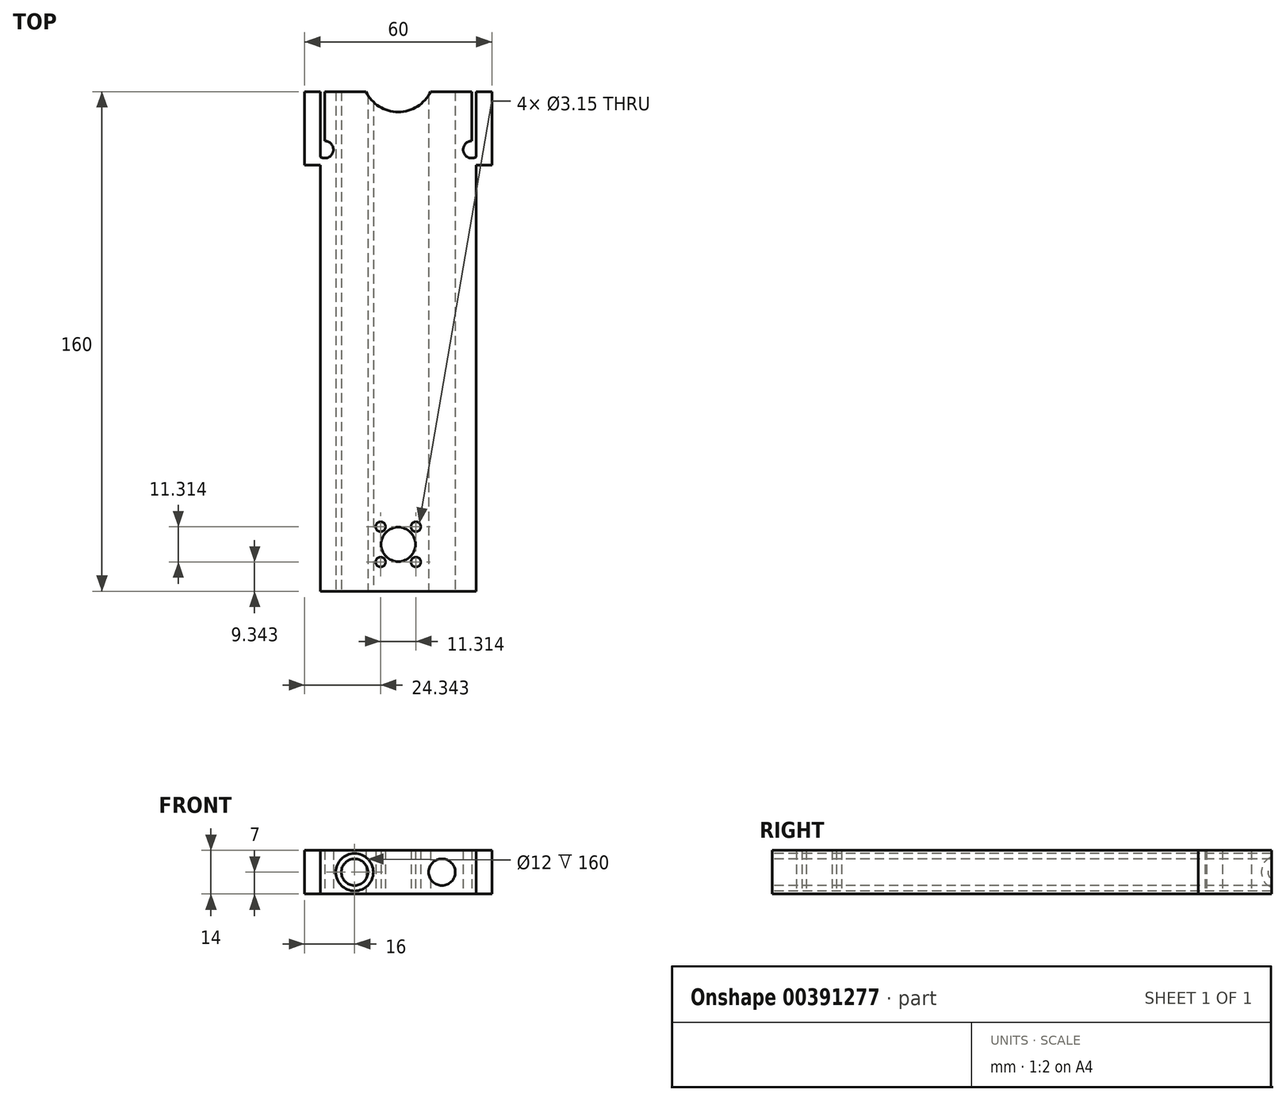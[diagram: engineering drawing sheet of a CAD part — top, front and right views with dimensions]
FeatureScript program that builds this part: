
annotation { "Feature Type Name" : "Feature", "Feature Type Description" : "" }
export const myFeature = defineFeature(function(context is Context, id is Id, definition is map)
    precondition{}
    {
        {
            var Q0;
            Q0=qCreatedBy(makeId("Top.planeOp"),FACE);
            var sketch = newSketch(context, id + "F0", { "sketchPlane" : qUnion([Q0])});
            skPoint(sketch, "E0", {"position": v(0, 0) * mm});
            skLineSegment(sketch, "E1.bottom", {"start": v(5.66, -5.66) * mm, "end": v(-5.66, -5.66) * mm, "construction": true});
            skLineSegment(sketch, "E1.top", {"start": v(5.66, 5.66) * mm, "end": v(-5.66, 5.66) * mm, "construction": true});
            skLineSegment(sketch, "E1.left", {"start": v(5.66, -5.66) * mm, "end": v(5.66, 5.66) * mm, "construction": true});
            skLineSegment(sketch, "E1.right", {"start": v(-5.66, -5.66) * mm, "end": v(-5.66, 5.66) * mm, "construction": true});
            skCircle(sketch, "E2", {"center": v(-5.66, 5.66) * mm, "radius": 1.57 * mm});
            skCircle(sketch, "E3", {"center": v(5.66, 5.66) * mm, "radius": 1.57 * mm});
            skCircle(sketch, "E4", {"center": v(5.66, -5.66) * mm, "radius": 1.57 * mm});
            skCircle(sketch, "E5", {"center": v(-5.66, -5.66) * mm, "radius": 1.57 * mm});
            skCircle(sketch, "E6", {"center": v(0, 0) * mm, "radius": 5.5 * mm});
            skPoint(sketch, "E7.startSnap0", {"position": v(0, 5.66) * mm});
            skLineSegment(sketch, "E8", {"start": v(0, -15) * mm, "end": v(25, -15) * mm});
            skLineSegment(sketch, "E9", {"start": v(25, -15) * mm, "end": v(25, 0) * mm});
            skLineSegment(sketch, "E10", {"start": v(25, 0) * mm, "end": v(25, 150) * mm});
            skLineSegment(sketch, "E11", {"start": v(25, 150) * mm, "end": v(0, 150) * mm});
            skLineSegment(sketch, "E12.MirrorCS", {"start": v(-25, 0) * mm, "end": v(-25, 150) * mm});
            skLineSegment(sketch, "E13.MirrorCS", {"start": v(-25, 150) * mm, "end": v(0, 150) * mm});
            skLineSegment(sketch, "E14.MirrorCS", {"start": v(0, -15) * mm, "end": v(-25, -15) * mm});
            skLineSegment(sketch, "E15.MirrorCS", {"start": v(-25, -15) * mm, "end": v(-25, 0) * mm});
            skLineSegment(sketch, "E16.bottom", {"start": v(23.55, 126.45) * mm, "end": v(-23.55, 126.45) * mm});
            skLineSegment(sketch, "E16.top", {"start": v(23.55, 173.55) * mm, "end": v(-23.55, 173.55) * mm});
            skLineSegment(sketch, "E16.left", {"start": v(23.55, 126.45) * mm, "end": v(23.55, 173.55) * mm});
            skLineSegment(sketch, "E16.right", {"start": v(-23.55, 126.45) * mm, "end": v(-23.55, 173.55) * mm});
            skPoint(sketch, "E16.middle", {"position": v(0, 150) * mm});
            skCircle(sketch, "E17", {"center": v(0, 150) * mm, "radius": 11.5 * mm});
            skCircle(sketch, "E18", {"center": v(-23.55, 126.45) * mm, "radius": 2.75 * mm});
            skCircle(sketch, "E19", {"center": v(23.55, 126.45) * mm, "radius": 2.75 * mm});
            skCircle(sketch, "E20", {"center": v(23.55, 173.55) * mm, "radius": 2.75 * mm});
            skCircle(sketch, "E21", {"center": v(-23.55, 173.55) * mm, "radius": 2.75 * mm});
            skLineSegment(sketch, "E22", {"start": v(-25, 145) * mm, "end": v(25, 145) * mm});
            skSolve(sketch);
        }
        {
            var Q0;
            Q0=makeQuery(id+"F0.imprint","IMPRINT",FACE,{"disambiguationData":[TD([[makeQuery(id+"F0.imprint","IMPRINT",EDGE,{"derivedFrom":sQuery(id+"F0.wireOp",EDGE,"E2")}),-1.0]])]});
            var Q1;
            {var subQ4=sQuery(id+"F0.wireOp",EDGE,"E19");var subQ12=sQuery(id+"F0.wireOp",EDGE,"E16.bottom");var subQ13=makeQuery(id+"F0.imprint","INTERSECT",VERTEX,{"derivedFrom":[subQ12,subQ4]});Q1=makeQuery(id+"F0.imprint","IMPRINT",FACE,{"disambiguationData":[TD([[makeQuery(id+"F0.imprint","IMPRINT",EDGE,{"disambiguationData":[TD([[subQ13,-1.0]])],"derivedFrom":subQ12}),-1.0]])]});}
            var Q2;
            {var subQ0=sQuery(id+"F0.wireOp",EDGE,"E22");var subQ1=sQuery(id+"F0.wireOp",EDGE,"E12.MirrorCS");var subQ2=makeQuery(id+"F0.imprint","INTERSECT",VERTEX,{"derivedFrom":[subQ1,subQ0]});Q2=makeQuery(id+"F0.imprint","IMPRINT",FACE,{"disambiguationData":[TD([[makeQuery(id+"F0.imprint","IMPRINT",EDGE,{"disambiguationData":[TD([[subQ2,1.0]])],"derivedFrom":subQ1}),-1.0]])]});}
            var Q3;
            {var subQ0=sQuery(id+"F0.wireOp",EDGE,"E22");var subQ1=sQuery(id+"F0.wireOp",EDGE,"E10");var subQ2=makeQuery(id+"F0.imprint","INTERSECT",VERTEX,{"derivedFrom":[subQ1,subQ0]});Q3=makeQuery(id+"F0.imprint","IMPRINT",FACE,{"disambiguationData":[TD([[makeQuery(id+"F0.imprint","IMPRINT",EDGE,{"disambiguationData":[TD([[subQ2,1.0]])],"derivedFrom":subQ1}),1.0]])]});}
            extrude(context, id + "F1", {"entities" : qUnion([Q0, Q1, Q2, Q3]), "depth" : 14 * mm});
        }
        {
            var Q0;
            Q0=makeQuery(id+"F1.opExtrude","SWEPT_FACE",FACE,{"disambiguationData":[OSD([sQuery(id+"F0.wireOp",EDGE,"E8"),sQuery(id+"F0.wireOp",EDGE,"E14.MirrorCS")])]});
            cPlane(context, id + "F2", {"entities" : qUnion([Q0]), "cplaneType" : CPlaneType.OFFSET, "offset" : 0 * mm, "oppositeDirection" : true, "width" : 150 * mm, "height" : 150 * mm});
        }
        {
            var Q0;
            Q0=qCreatedBy(id+"F2.planeOp",FACE);
            var sketch = newSketch(context, id + "F3", { "sketchPlane" : qUnion([Q0])});
            skCircle(sketch, "E23", {"center": v(14, 7) * mm, "radius": 4.25 * mm});
            skCircle(sketch, "E24", {"center": v(14, 7) * mm, "radius": 6 * mm});
            skCircle(sketch, "E25.MirrorC", {"center": v(-14, 7) * mm, "radius": 4.25 * mm});
            skCircle(sketch, "E26.MirrorC", {"center": v(-14, 7) * mm, "radius": 6 * mm});
            skSolve(sketch);
        }
        {
            var Q0;
            Q0=makeQuery(id+"F3.imprint","IMPRINT",FACE,{"disambiguationData":[TD([[makeQuery(id+"F3.imprint","IMPRINT",EDGE,{"derivedFrom":sQuery(id+"F3.wireOp",EDGE,"E25.MirrorC")}),-1.0]])]});
            var Q1;
            Q1=makeQuery(id+"F3.imprint","IMPRINT",FACE,{"disambiguationData":[TD([[makeQuery(id+"F3.imprint","IMPRINT",EDGE,{"derivedFrom":sQuery(id+"F3.wireOp",EDGE,"E23")}),1.0]])]});
            extrude(context, id + "F4", {"entities" : qUnion([Q0, Q1]), "operationType" : NewBodyOperationType.REMOVE, "oppositeDirection" : true, "depth" : 200 * mm});
        }
        {
            var Q0;
            Q0=qCreatedBy(makeId("Top.planeOp"),FACE);
            var sketch = newSketch(context, id + "F5", { "sketchPlane" : qUnion([Q0])});
            skLineSegment(sketch, "E27.bottom", {"start": v(-30, 121.45) * mm, "end": v(30, 121.45) * mm});
            skLineSegment(sketch, "E27.top", {"start": v(-30, 186.32) * mm, "end": v(30, 186.32) * mm});
            skLineSegment(sketch, "E27.left", {"start": v(-30, 121.45) * mm, "end": v(-30, 186.32) * mm});
            skLineSegment(sketch, "E27.right", {"start": v(30, 121.45) * mm, "end": v(30, 186.32) * mm});
            skPoint(sketch, "E27.middle", {"position": v(0, 153.89) * mm});
            skPoint(sketch, "E28.0", {"position": v(-25, 145) * mm});
            skPoint(sketch, "E29.0", {"position": v(25, 145) * mm});
            skLineSegment(sketch, "E30", {"start": v(-25, 145) * mm, "end": v(-30, 145) * mm});
            skLineSegment(sketch, "E31", {"start": v(25, 145) * mm, "end": v(30, 145) * mm});
            skLineSegment(sketch, "E32", {"start": v(25, 145) * mm, "end": v(25, 121.45) * mm});
            skLineSegment(sketch, "E33", {"start": v(-25, 121.45) * mm, "end": v(-25, 145) * mm});
            skSolve(sketch);
        }
        {
            var Q0;
            {var subQ4=sQuery(id+"F5.wireOp",EDGE,"E31");Q0=makeQuery(id+"F5.imprint","IMPRINT",FACE,{"disambiguationData":[TD([[makeQuery(id+"F5.imprint","IMPRINT",EDGE,{"derivedFrom":subQ4}),-1.0]])]});}
            var Q1;
            {var subQ4=sQuery(id+"F5.wireOp",EDGE,"E30");Q1=makeQuery(id+"F5.imprint","IMPRINT",FACE,{"disambiguationData":[TD([[makeQuery(id+"F5.imprint","IMPRINT",EDGE,{"derivedFrom":subQ4}),1.0]])]});}
            extrude(context, id + "F6", {"entities" : qUnion([Q0, Q1]), "operationType" : NewBodyOperationType.ADD, "depth" : 14 * mm});
        }
        {
            var Q0;
            {var subQ0=sQuery(id+"F0.wireOp",EDGE,"E19");var subQ1=sQuery(id+"F0.wireOp",EDGE,"E10");var subQ8=makeQuery(id+"F0.imprint","INTERSECT",VERTEX,{"disambiguationData":[OD(0.0)],"derivedFrom":[subQ1,subQ0]});Q0=makeQuery(id+"F0.imprint","IMPRINT",FACE,{"disambiguationData":[TD([[makeQuery(id+"F0.imprint","IMPRINT",EDGE,{"disambiguationData":[TD([[subQ8,-1.0]])],"derivedFrom":subQ1}),1.0]])]});}
            var Q1;
            {var subQ0=sQuery(id+"F0.wireOp",EDGE,"E19");var subQ1=sQuery(id+"F0.wireOp",EDGE,"E10");var subQ2=makeQuery(id+"F0.imprint","INTERSECT",VERTEX,{"disambiguationData":[OD(0.0)],"derivedFrom":[subQ1,subQ0]});Q1=makeQuery(id+"F0.imprint","IMPRINT",FACE,{"disambiguationData":[TD([[makeQuery(id+"F0.imprint","IMPRINT",EDGE,{"disambiguationData":[TD([[subQ2,-1.0]])],"derivedFrom":subQ1}),-1.0]])]});}
            var Q2;
            {var subQ0=sQuery(id+"F0.wireOp",EDGE,"E16.left");var subQ1=sQuery(id+"F0.wireOp",EDGE,"E16.bottom");var subQ2=makeQuery(id+"F0.imprint","INTERSECT",VERTEX,{"derivedFrom":[subQ1,subQ0]});Q2=makeQuery(id+"F0.imprint","IMPRINT",FACE,{"disambiguationData":[TD([[makeQuery(id+"F0.imprint","IMPRINT",EDGE,{"disambiguationData":[TD([[subQ2,-1.0]])],"derivedFrom":subQ1}),-1.0]])]});}
            var Q3;
            {var subQ0=sQuery(id+"F0.wireOp",EDGE,"E18");var subQ1=sQuery(id+"F0.wireOp",EDGE,"E12.MirrorCS");var subQ2=makeQuery(id+"F0.imprint","INTERSECT",VERTEX,{"disambiguationData":[OD(0.0)],"derivedFrom":[subQ1,subQ0]});Q3=makeQuery(id+"F0.imprint","IMPRINT",FACE,{"disambiguationData":[TD([[makeQuery(id+"F0.imprint","IMPRINT",EDGE,{"disambiguationData":[TD([[subQ2,-1.0]])],"derivedFrom":subQ1}),1.0]])]});}
            var Q4;
            {var subQ0=sQuery(id+"F0.wireOp",EDGE,"E18");var subQ1=sQuery(id+"F0.wireOp",EDGE,"E12.MirrorCS");var subQ8=makeQuery(id+"F0.imprint","INTERSECT",VERTEX,{"disambiguationData":[OD(0.0)],"derivedFrom":[subQ1,subQ0]});Q4=makeQuery(id+"F0.imprint","IMPRINT",FACE,{"disambiguationData":[TD([[makeQuery(id+"F0.imprint","IMPRINT",EDGE,{"disambiguationData":[TD([[subQ8,-1.0]])],"derivedFrom":subQ1}),-1.0]])]});}
            var Q5;
            {var subQ0=sQuery(id+"F0.wireOp",EDGE,"E16.right");var subQ1=sQuery(id+"F0.wireOp",EDGE,"E16.bottom");var subQ2=makeQuery(id+"F0.imprint","INTERSECT",VERTEX,{"derivedFrom":[subQ1,subQ0]});Q5=makeQuery(id+"F0.imprint","IMPRINT",FACE,{"disambiguationData":[TD([[makeQuery(id+"F0.imprint","IMPRINT",EDGE,{"disambiguationData":[TD([[subQ2,1.0]])],"derivedFrom":subQ1}),-1.0]])]});}
            extrude(context, id + "F7", {"entities" : qUnion([Q0, Q1, Q2, Q3, Q4, Q5]), "operationType" : NewBodyOperationType.REMOVE, "depth" : 25 * mm});
        }
    });
